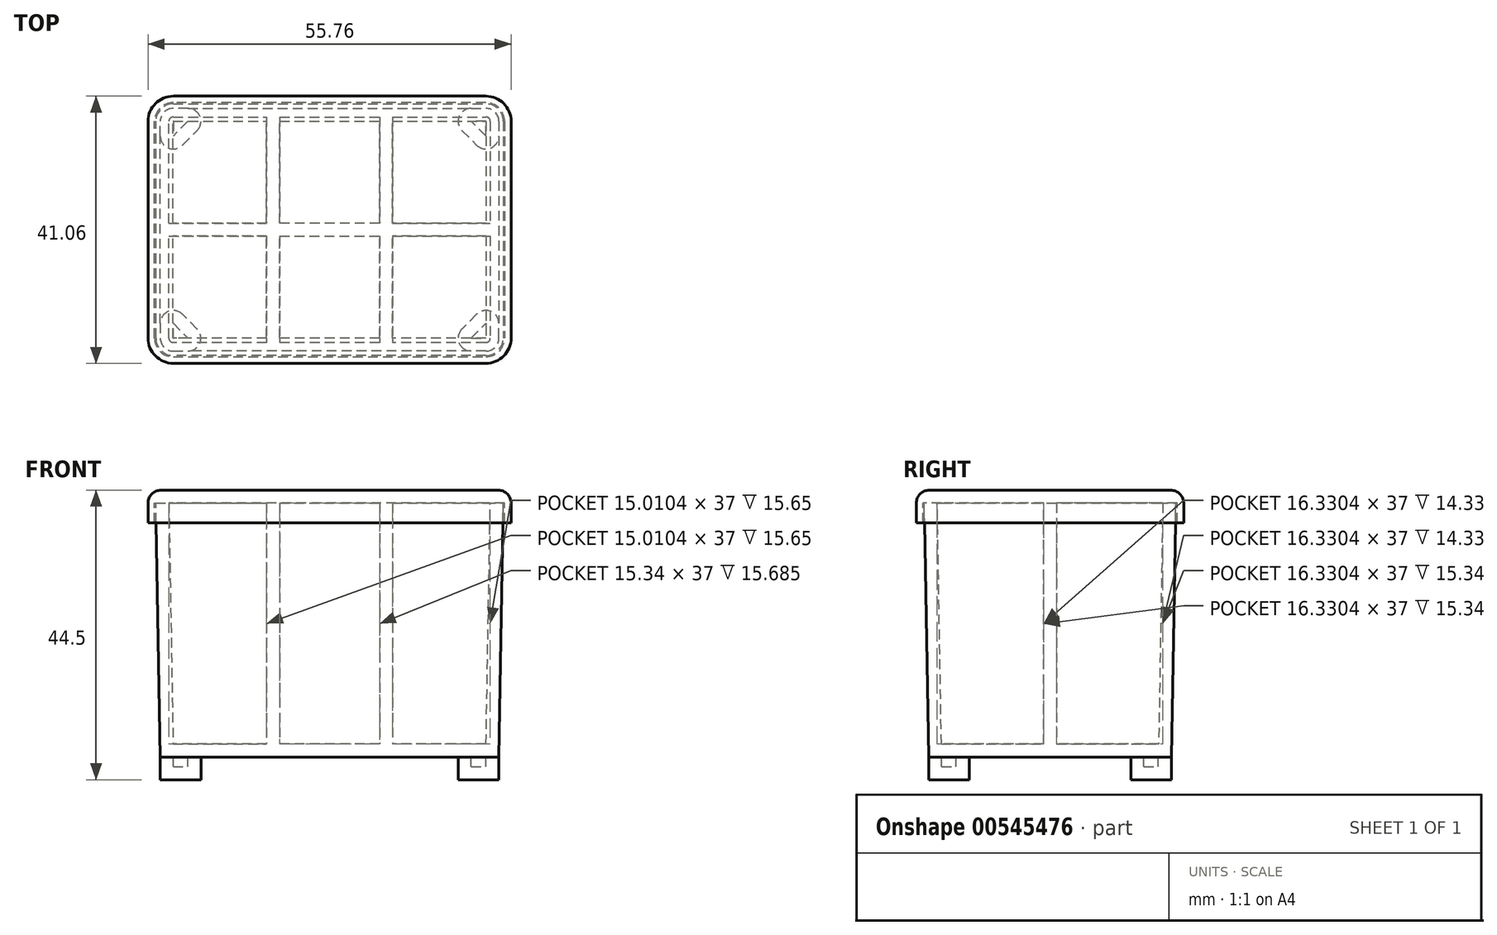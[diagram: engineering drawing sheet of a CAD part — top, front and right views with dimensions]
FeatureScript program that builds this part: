
annotation { "Feature Type Name" : "Feature", "Feature Type Description" : "" }
export const myFeature = defineFeature(function(context is Context, id is Id, definition is map)
    precondition{}
    {
        {
            var Q0;
            Q0=qCreatedBy(makeId("Top.planeOp"),FACE);
            var sketch = newSketch(context, id + "F0", { "sketchPlane" : qUnion([Q0])});
            skLineSegment(sketch, "E0.bottom", {"start": v(-21.76, 18.65) * mm, "end": v(-24, 18.65) * mm});
            skLineSegment(sketch, "E0.left", {"start": v(26, 16.65) * mm, "end": v(26, 14.4) * mm});
            skLineSegment(sketch, "E0.right", {"start": v(-26, -14.4) * mm, "end": v(-26, -16.65) * mm});
            skPoint(sketch, "E0.middle", {"position": v(0, 0) * mm});
            skPoint(sketch, "E1.visualSharp", {"position": v(-26, 18.65) * mm});
            skArc(sketch, "E1.filletArc", {"start": v(-24, 18.65) * mm, "mid": v(-25.41, 18.06) * mm, "end": v(-26, 16.65) * mm});
            skPoint(sketch, "E2.visualSharp", {"position": v(26, 18.65) * mm});
            skArc(sketch, "E2.filletArc", {"start": v(26, 16.65) * mm, "mid": v(25.41, 18.06) * mm, "end": v(24, 18.65) * mm});
            skPoint(sketch, "E3.visualSharp", {"position": v(26, -18.65) * mm});
            skArc(sketch, "E3.filletArc", {"start": v(24, -18.65) * mm, "mid": v(25.41, -18.06) * mm, "end": v(26, -16.65) * mm});
            skPoint(sketch, "E4.visualSharp", {"position": v(-26, -18.65) * mm});
            skLineSegment(sketch, "E5.0", {"start": v(-20.34, -15.24) * mm, "end": v(-22.59, -13) * mm});
            skLineSegment(sketch, "E6.0", {"start": v(-22.59, 13) * mm, "end": v(-20.34, 15.24) * mm});
            skLineSegment(sketch, "E7.0", {"start": v(22.59, -13) * mm, "end": v(20.34, -15.24) * mm});
            skLineSegment(sketch, "E8.0", {"start": v(20.34, 15.24) * mm, "end": v(22.59, 13) * mm});
            skPoint(sketch, "E9", {"position": v(-25.19, -9.43) * mm});
            skArc(sketch, "E10.filletArc", {"start": v(-22.59, -13) * mm, "mid": v(-24.77, -12.56) * mm, "end": v(-26, -14.4) * mm});
            skArc(sketch, "E11.filletArc", {"start": v(-21.76, -18.65) * mm, "mid": v(-19.9, -17.42) * mm, "end": v(-20.34, -15.24) * mm});
            skArc(sketch, "E12.filletArc", {"start": v(-20.34, 15.24) * mm, "mid": v(-19.9, 17.42) * mm, "end": v(-21.76, 18.65) * mm});
            skArc(sketch, "E13.filletArc", {"start": v(22.59, 13) * mm, "mid": v(24.77, 12.56) * mm, "end": v(26, 14.4) * mm});
            skLineSegment(sketch, "E14", {"start": v(21.76, 18.65) * mm, "end": v(24, 18.65) * mm});
            skLineSegment(sketch, "E15", {"start": v(26, -16.65) * mm, "end": v(26, -14.4) * mm});
            skLineSegment(sketch, "E16", {"start": v(24, -18.65) * mm, "end": v(21.76, -18.65) * mm});
            skLineSegment(sketch, "E17", {"start": v(-26, 14.4) * mm, "end": v(-26, 16.65) * mm});
            skArc(sketch, "E18.filletArc", {"start": v(-26, 14.4) * mm, "mid": v(-24.77, 12.56) * mm, "end": v(-22.59, 13) * mm});
            skArc(sketch, "E19.filletArc", {"start": v(20.34, -15.24) * mm, "mid": v(19.9, -17.42) * mm, "end": v(21.76, -18.65) * mm});
            skArc(sketch, "E20.filletArc", {"start": v(26, -14.4) * mm, "mid": v(24.77, -12.56) * mm, "end": v(22.59, -13) * mm});
            skArc(sketch, "E21.filletArc", {"start": v(21.76, 18.65) * mm, "mid": v(19.9, 17.42) * mm, "end": v(20.34, 15.24) * mm});
            skLineSegment(sketch, "E22", {"start": v(-21.76, 18.65) * mm, "end": v(21.76, 18.65) * mm});
            skLineSegment(sketch, "E23", {"start": v(26, 14.4) * mm, "end": v(26, -14.4) * mm});
            skLineSegment(sketch, "E24", {"start": v(21.76, -18.65) * mm, "end": v(-21.76, -18.65) * mm});
            skLineSegment(sketch, "E25", {"start": v(-26, 14.4) * mm, "end": v(-26, -14.4) * mm});
            skLineSegment(sketch, "E26", {"start": v(-24, -18.65) * mm, "end": v(-21.76, -18.65) * mm});
            skLineSegment(sketch, "E27", {"start": v(-24, -18.65) * mm, "end": v(-24, -18.65) * mm});
            skArc(sketch, "E28.filletArc", {"start": v(-26, -16.65) * mm, "mid": v(-25.41, -18.06) * mm, "end": v(-24, -18.65) * mm});
            skLineSegment(sketch, "E29.0", {"start": v(-26, 1) * mm, "end": v(-9.67, 1) * mm});
            skLineSegment(sketch, "E30.0", {"start": v(-26, -1) * mm, "end": v(-9.67, -1) * mm});
            skPoint(sketch, "E31.orphan", {"position": v(0, 18.65) * mm});
            skPoint(sketch, "E32.orphan", {"position": v(0, -18.65) * mm});
            skLineSegment(sketch, "E33.0", {"start": v(-9.67, 18.65) * mm, "end": v(-9.67, 1) * mm});
            skLineSegment(sketch, "E34.0", {"start": v(-7.67, 18.65) * mm, "end": v(-7.67, 1) * mm});
            skLineSegment(sketch, "E35.0", {"start": v(7.67, 18.65) * mm, "end": v(7.67, 1) * mm});
            skLineSegment(sketch, "E36.0", {"start": v(9.67, 18.65) * mm, "end": v(9.67, 1) * mm});
            skLineSegment(sketch, "E37.trimOffspring", {"start": v(-7.67, -1) * mm, "end": v(7.67, -1) * mm});
            skPoint(sketch, "E38.orphan", {"position": v(26, 0) * mm});
            skLineSegment(sketch, "E39.trimOffspring", {"start": v(7.67, -1) * mm, "end": v(7.67, -18.65) * mm});
            skLineSegment(sketch, "E40.trimOffspring", {"start": v(9.67, -1) * mm, "end": v(26, -1) * mm});
            skLineSegment(sketch, "E41.trimOffspring", {"start": v(-7.67, -1) * mm, "end": v(-7.67, -18.65) * mm});
            skLineSegment(sketch, "E42.trimOffspring", {"start": v(-9.67, -1) * mm, "end": v(-9.67, -18.65) * mm});
            skLineSegment(sketch, "E43.trimOffspring", {"start": v(-7.67, 1) * mm, "end": v(7.67, 1) * mm});
            skPoint(sketch, "E44.start.orphan", {"position": v(-26, 0) * mm});
            skLineSegment(sketch, "E45.trimOffspring", {"start": v(9.67, -1) * mm, "end": v(9.67, -18.65) * mm});
            skLineSegment(sketch, "E46.trimOffspring", {"start": v(9.67, 1) * mm, "end": v(26, 1) * mm});
            skSolve(sketch);
        }
        {
            var Q0;
            Q0=makeQuery(id+"F0.imprint","IMPRINT",FACE,{"disambiguationData":[TD([[makeQuery(id+"F0.imprint","IMPRINT",EDGE,{"derivedFrom":sQuery(id+"F0.wireOp",EDGE,"E0.bottom")}),1.0]])]});
            var Q1;
            Q1=makeQuery(id+"F0.imprint","IMPRINT",FACE,{"disambiguationData":[TD([[makeQuery(id+"F0.imprint","IMPRINT",EDGE,{"derivedFrom":sQuery(id+"F0.wireOp",EDGE,"E0.left")}),-1.0]])]});
            var Q2;
            Q2=makeQuery(id+"F0.imprint","IMPRINT",FACE,{"disambiguationData":[TD([[makeQuery(id+"F0.imprint","IMPRINT",EDGE,{"derivedFrom":sQuery(id+"F0.wireOp",EDGE,"E3.filletArc")}),1.0]])]});
            var Q3;
            Q3=makeQuery(id+"F0.imprint","IMPRINT",FACE,{"disambiguationData":[TD([[makeQuery(id+"F0.imprint","IMPRINT",EDGE,{"derivedFrom":sQuery(id+"F0.wireOp",EDGE,"E0.right")}),1.0]])]});
            extrude(context, id + "F1", {"entities" : qUnion([Q0, Q1, Q2, Q3]), "oppositeDirection" : true, "depth" : 3.5 * mm, "offsetDistance" : 25 * mm});
        }
        {
            var Q0;
            Q0=qSketchRegion(id+"F0",true);
            var Q1;
            Q1=makeQuery(id+"F1.opExtrude","CAP_FACE",FACE,{"disambiguationData":[OSD([sQuery(id+"F0.wireOp",EDGE,"E0.right"),sQuery(id+"F0.wireOp",EDGE,"E5.0"),sQuery(id+"F0.wireOp",EDGE,"E10.filletArc"),sQuery(id+"F0.wireOp",EDGE,"E11.filletArc"),sQuery(id+"F0.wireOp",EDGE,"E26"),sQuery(id+"F0.wireOp",EDGE,"E28.filletArc")])],"isStart":true});
            extrude(context, id + "F2", {"entities" : qUnion([Q0, Q1]), "operationType" : NewBodyOperationType.ADD, "depth" : 39 * mm, "offsetDistance" : 25 * mm, "hasDraft" : true, "draftAngle" : 1 * degree});
        }
        {
            var Q0;
            Q0=makeQuery(id+"F2.opExtrude","CAP_FACE",FACE,{"disambiguationData":[OSD([sQuery(id+"F0.wireOp",EDGE,"E0.bottom"),sQuery(id+"F0.wireOp",EDGE,"E0.left"),sQuery(id+"F0.wireOp",EDGE,"E0.right"),sQuery(id+"F0.wireOp",EDGE,"E1.filletArc"),sQuery(id+"F0.wireOp",EDGE,"E2.filletArc"),sQuery(id+"F0.wireOp",EDGE,"E3.filletArc"),sQuery(id+"F0.wireOp",EDGE,"E14"),sQuery(id+"F0.wireOp",EDGE,"E15"),sQuery(id+"F0.wireOp",EDGE,"E16"),sQuery(id+"F0.wireOp",EDGE,"E17"),sQuery(id+"F0.wireOp",EDGE,"E22"),sQuery(id+"F0.wireOp",EDGE,"E23"),sQuery(id+"F0.wireOp",EDGE,"E24"),sQuery(id+"F0.wireOp",EDGE,"E25"),sQuery(id+"F0.wireOp",EDGE,"E26"),sQuery(id+"F0.wireOp",EDGE,"E28.filletArc")])],"isStart":false});
            shell(context, id + "F3", {"entities" : qUnion([Q0]), "thickness" : 2 * mm});
        }
        {
            var Q0;
            {var subQ2=sQuery(id+"F0.wireOp",EDGE,"E29.0");Q0=makeQuery(id+"F0.imprint","IMPRINT",FACE,{"disambiguationData":[TD([[makeQuery(id+"F0.imprint","IMPRINT",EDGE,{"derivedFrom":subQ2}),-1.0]])]});}
            extrude(context, id + "F4", {"entities" : qUnion([Q0]), "operationType" : NewBodyOperationType.ADD, "depth" : 39 * mm, "offsetDistance" : 25 * mm});
        }
        {
            var Q0;
            Q0=makeQuery(id+"F0.imprint","IMPRINT",FACE,{"disambiguationData":[TD([[makeQuery(id+"F0.imprint","IMPRINT",EDGE,{"derivedFrom":sQuery(id+"F0.wireOp",EDGE,"E0.bottom")}),1.0]])]});
            var Q1;
            Q1=makeQuery(id+"F0.imprint","IMPRINT",FACE,{"disambiguationData":[TD([[makeQuery(id+"F0.imprint","IMPRINT",EDGE,{"derivedFrom":sQuery(id+"F0.wireOp",EDGE,"E0.left")}),-1.0]])]});
            var Q2;
            Q2=makeQuery(id+"F0.imprint","IMPRINT",FACE,{"disambiguationData":[TD([[makeQuery(id+"F0.imprint","IMPRINT",EDGE,{"derivedFrom":sQuery(id+"F0.wireOp",EDGE,"E3.filletArc")}),1.0]])]});
            var Q3;
            Q3=makeQuery(id+"F0.imprint","IMPRINT",FACE,{"disambiguationData":[TD([[makeQuery(id+"F0.imprint","IMPRINT",EDGE,{"derivedFrom":sQuery(id+"F0.wireOp",EDGE,"E0.right")}),1.0]])]});
            extrude(context, id + "F5", {"entities" : qUnion([Q0, Q1, Q2, Q3]), "operationType" : NewBodyOperationType.ADD, "depth" : 2 * mm, "offsetDistance" : 25 * mm});
        }
        {
            var Q0;
            {var subQ0=sQuery(id+"F0.wireOp",EDGE,"E25");var subQ1=sQuery(id+"F0.wireOp",EDGE,"E24");var subQ2=sQuery(id+"F0.wireOp",EDGE,"E23");var subQ3=sQuery(id+"F0.wireOp",EDGE,"E22");Q0=makeQuery(id+"F4.boolean.opBoolean","MERGE",FACE,{"derivedFrom":[makeQuery(id+"F2.opExtrude","CAP_FACE",FACE,{"disambiguationData":[OSD([sQuery(id+"F0.wireOp",EDGE,"E0.bottom"),sQuery(id+"F0.wireOp",EDGE,"E0.left"),sQuery(id+"F0.wireOp",EDGE,"E0.right"),sQuery(id+"F0.wireOp",EDGE,"E1.filletArc"),sQuery(id+"F0.wireOp",EDGE,"E2.filletArc"),sQuery(id+"F0.wireOp",EDGE,"E3.filletArc"),sQuery(id+"F0.wireOp",EDGE,"E14"),sQuery(id+"F0.wireOp",EDGE,"E15"),sQuery(id+"F0.wireOp",EDGE,"E16"),sQuery(id+"F0.wireOp",EDGE,"E17"),subQ3,subQ2,subQ1,subQ0,sQuery(id+"F0.wireOp",EDGE,"E26"),sQuery(id+"F0.wireOp",EDGE,"E28.filletArc")])],"isStart":false}),makeQuery(id+"F4.opExtrude","CAP_FACE",FACE,{"disambiguationData":[OSD([subQ3,subQ2,subQ1,subQ0,sQuery(id+"F0.wireOp",EDGE,"E29.0"),sQuery(id+"F0.wireOp",EDGE,"E30.0"),sQuery(id+"F0.wireOp",EDGE,"E33.0"),sQuery(id+"F0.wireOp",EDGE,"E34.0"),sQuery(id+"F0.wireOp",EDGE,"E35.0"),sQuery(id+"F0.wireOp",EDGE,"E36.0"),sQuery(id+"F0.wireOp",EDGE,"E37.trimOffspring"),sQuery(id+"F0.wireOp",EDGE,"E39.trimOffspring"),sQuery(id+"F0.wireOp",EDGE,"E40.trimOffspring"),sQuery(id+"F0.wireOp",EDGE,"E41.trimOffspring"),sQuery(id+"F0.wireOp",EDGE,"E42.trimOffspring"),sQuery(id+"F0.wireOp",EDGE,"E43.trimOffspring"),sQuery(id+"F0.wireOp",EDGE,"E45.trimOffspring"),sQuery(id+"F0.wireOp",EDGE,"E46.trimOffspring")])],"isStart":false})]});}
            var sketch = newSketch(context, id + "F6", { "sketchPlane" : qUnion([Q0])});
            skLineSegment(sketch, "E47.0", {"start": v(-24, -19.33) * mm, "end": v(24, -19.33) * mm});
            skArc(sketch, "E47.1", {"start": v(24, -19.33) * mm, "mid": v(25.9, -18.55) * mm, "end": v(26.68, -16.65) * mm});
            skLineSegment(sketch, "E47.2", {"start": v(26.68, 16.65) * mm, "end": v(26.68, -16.65) * mm});
            skArc(sketch, "E47.3", {"start": v(26.68, 16.65) * mm, "mid": v(25.9, 18.55) * mm, "end": v(24, 19.33) * mm});
            skLineSegment(sketch, "E47.4", {"start": v(24, 19.33) * mm, "end": v(-24, 19.33) * mm});
            skArc(sketch, "E47.5", {"start": v(-24, 19.33) * mm, "mid": v(-25.9, 18.55) * mm, "end": v(-26.68, 16.65) * mm});
            skLineSegment(sketch, "E47.6", {"start": v(-26.68, -16.65) * mm, "end": v(-26.68, 16.65) * mm});
            skArc(sketch, "E47.7", {"start": v(-26.68, -16.65) * mm, "mid": v(-25.9, -18.55) * mm, "end": v(-24, -19.33) * mm});
            skSolve(sketch);
        }
        {
            var Q0;
            Q0 = qSketchRegion(id + "F6", true);
            extrude(context, id + "F7", {"entities" : qUnion([Q0]), "depth" : 2 * mm, "offsetDistance" : 25 * mm});
        }
        {
            var Q0;
            Q0=makeQuery(id+"F6.imprint","IMPRINT",FACE,{"disambiguationData":[TD([[makeQuery(id+"F6.imprint","IMPRINT",EDGE,{"derivedFrom":sQuery(id+"F6.wireOp",EDGE,"E47.0")}),1.0]])]});
            var sketch = newSketch(context, id + "F8", { "sketchPlane" : qUnion([Q0])});
            skArc(sketch, "E48.0", {"start": v(-27.88, -16.65) * mm, "mid": v(-26.74, -19.4) * mm, "end": v(-24, -20.53) * mm});
            skLineSegment(sketch, "E48.1", {"start": v(-27.88, -16.65) * mm, "end": v(-27.88, 16.65) * mm});
            skLineSegment(sketch, "E48.2", {"start": v(-24, -20.53) * mm, "end": v(24, -20.53) * mm});
            skArc(sketch, "E48.3", {"start": v(-24, 20.53) * mm, "mid": v(-26.74, 19.4) * mm, "end": v(-27.88, 16.65) * mm});
            skArc(sketch, "E48.4", {"start": v(24, -20.53) * mm, "mid": v(26.74, -19.4) * mm, "end": v(27.88, -16.65) * mm});
            skLineSegment(sketch, "E48.5", {"start": v(27.88, 16.65) * mm, "end": v(27.88, -16.65) * mm});
            skArc(sketch, "E48.6", {"start": v(27.88, 16.65) * mm, "mid": v(26.74, 19.4) * mm, "end": v(24, 20.53) * mm});
            skLineSegment(sketch, "E48.7", {"start": v(24, 20.53) * mm, "end": v(-24, 20.53) * mm});
            skSolve(sketch);
        }
        {
            var Q0;
            Q0=makeQuery(id+"F8.imprint","IMPRINT",FACE,{"disambiguationData":[TD([[makeQuery(id+"F8.imprint","IMPRINT",EDGE,{"derivedFrom":sQuery(id+"F8.wireOp",EDGE,"E48.0")}),1.0]])]});
            extrude(context, id + "F9", {"entities" : qUnion([Q0]), "operationType" : NewBodyOperationType.ADD, "depth" : 2 * mm, "offsetDistance" : 25 * mm});
        }
        {
            var Q0;
            Q0=makeQuery(id+"F6.imprint","IMPRINT",FACE,{"disambiguationData":[TD([[makeQuery(id+"F6.imprint","IMPRINT",EDGE,{"derivedFrom":sQuery(id+"F6.wireOp",EDGE,"E47.0")}),1.0]])]});
            var sketch = newSketch(context, id + "F10", { "sketchPlane" : qUnion([Q0])});
            skLineSegment(sketch, "E49.0", {"start": v(-24, -19.33) * mm, "end": v(24, -19.33) * mm});
            skArc(sketch, "E49.1", {"start": v(24, -19.33) * mm, "mid": v(25.9, -18.55) * mm, "end": v(26.68, -16.65) * mm});
            skLineSegment(sketch, "E49.2", {"start": v(26.68, 16.65) * mm, "end": v(26.68, -16.65) * mm});
            skArc(sketch, "E49.3", {"start": v(26.68, 16.65) * mm, "mid": v(25.9, 18.55) * mm, "end": v(24, 19.33) * mm});
            skLineSegment(sketch, "E49.4", {"start": v(24, 19.33) * mm, "end": v(-24, 19.33) * mm});
            skArc(sketch, "E49.5", {"start": v(-24, 19.33) * mm, "mid": v(-25.9, 18.55) * mm, "end": v(-26.68, 16.65) * mm});
            skLineSegment(sketch, "E49.6", {"start": v(-26.68, -16.65) * mm, "end": v(-26.68, 16.65) * mm});
            skArc(sketch, "E49.7", {"start": v(-26.68, -16.65) * mm, "mid": v(-25.9, -18.55) * mm, "end": v(-24, -19.33) * mm});
            skArc(sketch, "E50.0", {"start": v(-26.88, -16.65) * mm, "mid": v(-26.04, -18.69) * mm, "end": v(-24, -19.53) * mm});
            skLineSegment(sketch, "E50.1", {"start": v(-26.88, -16.65) * mm, "end": v(-26.88, 16.65) * mm});
            skLineSegment(sketch, "E50.2", {"start": v(-24, -19.53) * mm, "end": v(24, -19.53) * mm});
            skArc(sketch, "E50.3", {"start": v(-24, 19.53) * mm, "mid": v(-26.04, 18.69) * mm, "end": v(-26.88, 16.65) * mm});
            skArc(sketch, "E50.4", {"start": v(24, -19.53) * mm, "mid": v(26.04, -18.69) * mm, "end": v(26.88, -16.65) * mm});
            skLineSegment(sketch, "E50.5", {"start": v(26.88, 16.65) * mm, "end": v(26.88, -16.65) * mm});
            skArc(sketch, "E50.6", {"start": v(26.88, 16.65) * mm, "mid": v(26.04, 18.69) * mm, "end": v(24, 19.53) * mm});
            skLineSegment(sketch, "E50.7", {"start": v(24, 19.53) * mm, "end": v(-24, 19.53) * mm});
            skArc(sketch, "E51.0", {"start": v(27.88, 16.65) * mm, "mid": v(26.74, 19.4) * mm, "end": v(24, 20.53) * mm});
            skLineSegment(sketch, "E51.1", {"start": v(27.88, 16.65) * mm, "end": v(27.88, -16.65) * mm});
            skLineSegment(sketch, "E51.2", {"start": v(24, 20.53) * mm, "end": v(-24, 20.53) * mm});
            skArc(sketch, "E51.3", {"start": v(24, -20.53) * mm, "mid": v(26.74, -19.4) * mm, "end": v(27.88, -16.65) * mm});
            skArc(sketch, "E51.4", {"start": v(-24, 20.53) * mm, "mid": v(-26.74, 19.4) * mm, "end": v(-27.88, 16.65) * mm});
            skLineSegment(sketch, "E51.5", {"start": v(-27.88, -16.65) * mm, "end": v(-27.88, 16.65) * mm});
            skArc(sketch, "E51.6", {"start": v(-27.88, -16.65) * mm, "mid": v(-26.74, -19.4) * mm, "end": v(-24, -20.53) * mm});
            skLineSegment(sketch, "E51.7", {"start": v(-24, -20.53) * mm, "end": v(24, -20.53) * mm});
            skSolve(sketch);
        }
        {
            var Q0;
            Q0=makeQuery(id+"F10.imprint","IMPRINT",FACE,{"disambiguationData":[TD([[makeQuery(id+"F10.imprint","IMPRINT",EDGE,{"derivedFrom":sQuery(id+"F10.wireOp",EDGE,"E50.0")}),-1.0]])]});
            extrude(context, id + "F11", {"entities" : qUnion([Q0]), "operationType" : NewBodyOperationType.ADD, "oppositeDirection" : true, "depth" : 3 * mm, "offsetDistance" : 25 * mm});
        }
        {
            var Q0;
            {var subQ0=sQuery(id+"F6.wireOp",EDGE,"E47.7");var subQ1=sQuery(id+"F6.wireOp",EDGE,"E47.6");var subQ2=sQuery(id+"F6.wireOp",EDGE,"E47.5");var subQ3=sQuery(id+"F6.wireOp",EDGE,"E47.4");var subQ4=sQuery(id+"F6.wireOp",EDGE,"E47.3");var subQ5=sQuery(id+"F6.wireOp",EDGE,"E47.2");var subQ6=sQuery(id+"F6.wireOp",EDGE,"E47.1");var subQ7=sQuery(id+"F6.wireOp",EDGE,"E47.0");Q0=makeQuery(id+"F9.boolean.opBoolean","MERGE",FACE,{"derivedFrom":[makeQuery(id+"F7.opExtrude","CAP_FACE",FACE,{"disambiguationData":[OSD([subQ7,subQ6,subQ5,subQ4,subQ3,subQ2,subQ1,subQ0])],"isStart":false}),makeQuery(id+"F9.opExtrude","CAP_FACE",FACE,{"disambiguationData":[OSD([subQ7,subQ6,subQ5,subQ4,subQ3,subQ2,subQ1,subQ0,sQuery(id+"F8.wireOp",EDGE,"E48.0"),sQuery(id+"F8.wireOp",EDGE,"E48.1"),sQuery(id+"F8.wireOp",EDGE,"E48.2"),sQuery(id+"F8.wireOp",EDGE,"E48.3"),sQuery(id+"F8.wireOp",EDGE,"E48.4"),sQuery(id+"F8.wireOp",EDGE,"E48.5"),sQuery(id+"F8.wireOp",EDGE,"E48.6"),sQuery(id+"F8.wireOp",EDGE,"E48.7")])],"isStart":false})]});}
            fillet(context, id + "F12", {"entities" : qUnion([Q0]), "radius" : 2 * mm, "tangentPropagation" : true, "allowEdgeOverflow" : false});
        }
    });
